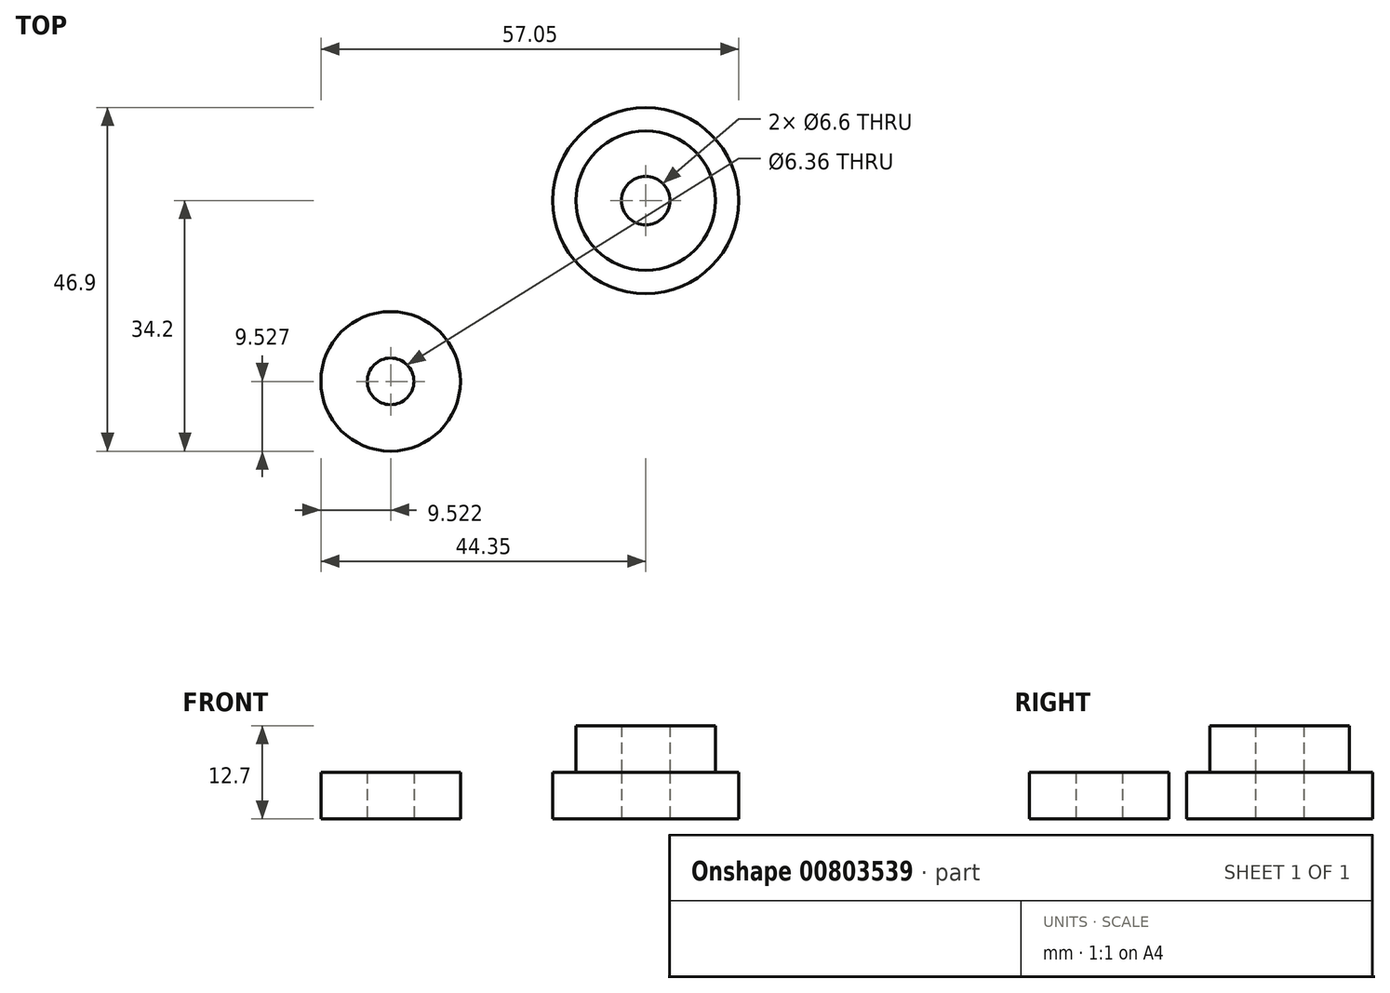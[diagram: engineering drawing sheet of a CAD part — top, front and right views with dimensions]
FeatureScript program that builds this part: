
annotation { "Feature Type Name" : "Feature", "Feature Type Description" : "" }
export const myFeature = defineFeature(function(context is Context, id is Id, definition is map)
    precondition{}
    {
        {
            var Q0;
            Q0=qCreatedBy(makeId("Top.planeOp"),FACE);
            var sketch = newSketch(context, id + "F0", { "sketchPlane" : qUnion([Q0])});
            skCircle(sketch, "E0", {"center": v(0, 0) * mm, "radius": 12.7 * mm});
            skCircle(sketch, "E1", {"center": v(0, 0) * mm, "radius": 3.3 * mm});
            skSolve(sketch);
        }
        {
            var Q0;
            Q0 = qSketchRegion(id + "F0", true);
            extrude(context, id + "F1", {"entities" : qUnion([Q0]), "depth" : 6.35 * mm, "offsetDistance" : 25.4 * mm});
        }
        {
            var Q0;
            Q0=makeQuery(id+"F1.opExtrude","CAP_FACE",FACE,{"disambiguationData":[OSD([sQuery(id+"F0.wireOp",EDGE,"E0")])],"isStart":false});
            var sketch = newSketch(context, id + "F2", { "sketchPlane" : qUnion([Q0])});
            skCircle(sketch, "E2", {"center": v(0, 0) * mm, "radius": 9.53 * mm});
            skCircle(sketch, "E3", {"center": v(0, 0) * mm, "radius": 3.3 * mm});
            skSolve(sketch);
        }
        {
            var Q0;
            Q0=qCreatedBy(makeId("Top.planeOp"),FACE);
            var sketch = newSketch(context, id + "F3", { "sketchPlane" : qUnion([Q0])});
            skCircle(sketch, "E4", {"center": v(-34.83, -24.67) * mm, "radius": 9.53 * mm});
            skCircle(sketch, "E5", {"center": v(-34.83, -24.67) * mm, "radius": 3.18 * mm});
            skSolve(sketch);
        }
        {
            var Q0;
            Q0=makeQuery(id+"F3.imprint","IMPRINT",FACE,{"disambiguationData":[TD([[makeQuery(id+"F3.imprint","IMPRINT",EDGE,{"derivedFrom":sQuery(id+"F3.wireOp",EDGE,"E4")}),1.0]])]});
            extrude(context, id + "F4", {"entities" : qUnion([Q0]), "depth" : 6.35 * mm, "offsetDistance" : 25.4 * mm});
        }
        {
            var Q0;
            Q0=makeQuery(id+"F2.imprint","IMPRINT",FACE,{"disambiguationData":[TD([[makeQuery(id+"F2.imprint","IMPRINT",EDGE,{"derivedFrom":sQuery(id+"F2.wireOp",EDGE,"E2")}),1.0]])]});
            extrude(context, id + "F5", {"entities" : qUnion([Q0]), "depth" : 6.35 * mm, "offsetDistance" : 25.4 * mm});
        }
    });
